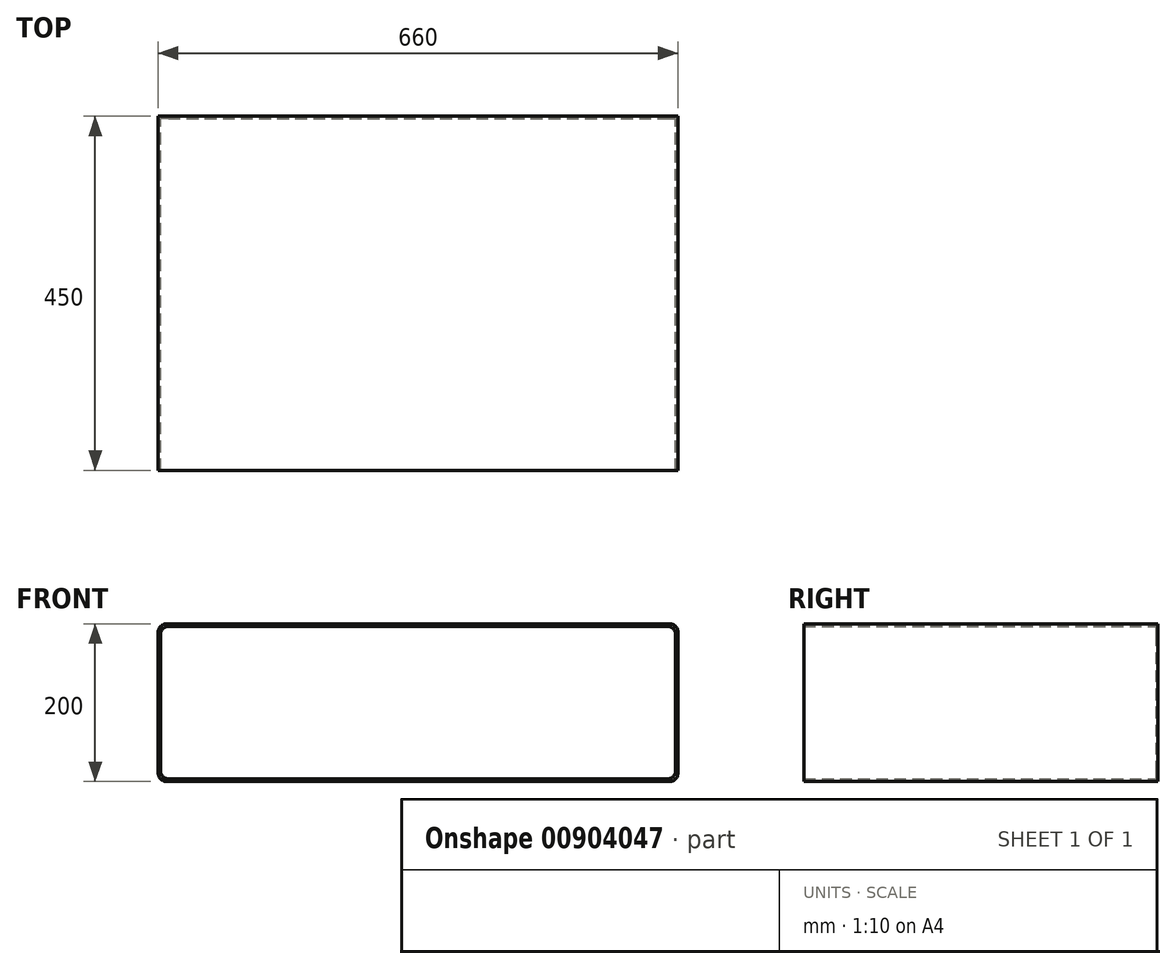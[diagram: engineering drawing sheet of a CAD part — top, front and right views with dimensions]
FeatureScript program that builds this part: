
annotation { "Feature Type Name" : "Feature", "Feature Type Description" : "" }
export const myFeature = defineFeature(function(context is Context, id is Id, definition is map)
    precondition{}
    {
        {
            assignVariable(context, id + "F0", {"name" : "Length", "anyValue" : 900});
        }
        {
            var Q0;
            Q0=qCreatedBy(makeId("Top.planeOp"),FACE);
            var sketch = newSketch(context, id + "F1", { "sketchPlane" : qUnion([Q0])});
            skLineSegment(sketch, "E0.bottom", {"start": v(-350, 450) * mm, "end": v(350, 450) * mm, "construction": true});
            skLineSegment(sketch, "E0.top", {"start": v(-350, -450) * mm, "end": v(350, -450) * mm, "construction": true});
            skLineSegment(sketch, "E0.left", {"start": v(-350, 450) * mm, "end": v(-350, -450) * mm, "construction": true});
            skLineSegment(sketch, "E0.right", {"start": v(350, 450) * mm, "end": v(350, -450) * mm, "construction": true});
            skLineSegment(sketch, "E1", {"start": v(-350, 0) * mm, "end": v(350, 0) * mm, "construction": true});
            skLineSegment(sketch, "E2", {"start": v(0, 450) * mm, "end": v(0, 0) * mm, "construction": true});
            skLineSegment(sketch, "E3", {"start": v(0, 0) * mm, "end": v(0, -450) * mm, "construction": true});
            skSolve(sketch);
        }
        {
            var Q0;
            Q0=qCreatedBy(makeId("Front.planeOp"),FACE);
            var sketch = newSketch(context, id + "F2", { "sketchPlane" : qUnion([Q0])});
            skLineSegment(sketch, "E4.bottom", {"start": v(-350, 300) * mm, "end": v(350, 300) * mm, "construction": true});
            skLineSegment(sketch, "E4.top", {"start": v(-350, -300) * mm, "end": v(350, -300) * mm, "construction": true});
            skLineSegment(sketch, "E4.left", {"start": v(-350, 300) * mm, "end": v(-350, -300) * mm, "construction": true});
            skLineSegment(sketch, "E4.right", {"start": v(350, 300) * mm, "end": v(350, -300) * mm, "construction": true});
            skLineSegment(sketch, "E5", {"start": v(0, 300) * mm, "end": v(0, -300) * mm, "construction": true});
            skSolve(sketch);
        }
        {
            var Q0;
            Q0=qCreatedBy(makeId("Front.planeOp"),FACE);
            var sketch = newSketch(context, id + "F3", { "sketchPlane" : qUnion([Q0])});
            skLineSegment(sketch, "E6.bottom", {"start": v(-330, 0) * mm, "end": v(330, 0) * mm});
            skLineSegment(sketch, "E6.top", {"start": v(-330, -200) * mm, "end": v(330, -200) * mm});
            skLineSegment(sketch, "E6.left", {"start": v(-330, 0) * mm, "end": v(-330, -200) * mm});
            skLineSegment(sketch, "E6.right", {"start": v(330, 0) * mm, "end": v(330, -200) * mm});
            skSolve(sketch);
        }
        {
            var Q0;
            Q0=makeQuery(id+"F3.imprint","IMPRINT",FACE,{"disambiguationData":[TD([[makeQuery(id+"F3.imprint","IMPRINT",EDGE,{"derivedFrom":sQuery(id+"F3.wireOp",EDGE,"E6.bottom")}),-1.0]])]});
            extrude(context, id + "F4", {"entities" : qUnion([Q0]), "depth" : (getVariable(context, 'Length') / 2) * mm, "offsetDistance" : 25 * mm});
        }
        {
            var Q0;
            Q0=makeQuery(id+"F4.opExtrude","CAP_FACE",FACE,{"disambiguationData":[OSD([sQuery(id+"F3.wireOp",EDGE,"E6.bottom"),sQuery(id+"F3.wireOp",EDGE,"E6.top"),sQuery(id+"F3.wireOp",EDGE,"E6.left"),sQuery(id+"F3.wireOp",EDGE,"E6.right")])],"isStart":false});
            shell(context, id + "F5", {"entities" : qUnion([Q0]), "thickness" : 3 * mm});
        }
        {
            var Q0;
            Q0=makeQuery(id+"F4.opExtrude","SWEPT_EDGE",EDGE,{"disambiguationData":[OSD([sQuery(id+"F3.wireOp",EDGE,"E6.top"),sQuery(id+"F3.wireOp",EDGE,"E6.right")])]});
            var Q1;
            Q1=makeQuery(id+"F4.opExtrude","SWEPT_EDGE",EDGE,{"disambiguationData":[OSD([sQuery(id+"F3.wireOp",EDGE,"E6.bottom"),sQuery(id+"F3.wireOp",EDGE,"E6.right")])]});
            fillet(context, id + "F6", {"entities" : qUnion([Q0, Q1]), "radius" : 10 * mm, "tangentPropagation" : true, "allowEdgeOverflow" : false});
        }
        {
            var Q0;
            Q0=makeQuery(id+"F5.opShell","OFFSET_EDGE",EDGE,{"disambiguationData":[OSD([sQuery(id+"F3.wireOp",EDGE,"E6.top"),sQuery(id+"F3.wireOp",EDGE,"E6.right")])]});
            var Q1;
            Q1=makeQuery(id+"F5.opShell","OFFSET_EDGE",EDGE,{"disambiguationData":[OSD([sQuery(id+"F3.wireOp",EDGE,"E6.bottom"),sQuery(id+"F3.wireOp",EDGE,"E6.right")])]});
            var Q2;
            Q2=makeQuery(id+"F5.opShell","OFFSET_EDGE",EDGE,{"disambiguationData":[OSD([sQuery(id+"F3.wireOp",EDGE,"E6.top"),sQuery(id+"F3.wireOp",EDGE,"E6.left")])]});
            var Q3;
            Q3=makeQuery(id+"F5.opShell","OFFSET_EDGE",EDGE,{"disambiguationData":[OSD([sQuery(id+"F3.wireOp",EDGE,"E6.bottom"),sQuery(id+"F3.wireOp",EDGE,"E6.left")])]});
            fillet(context, id + "F7", {"entities" : qUnion([Q0, Q1, Q2, Q3]), "radius" : 10 * mm, "tangentPropagation" : true, "allowEdgeOverflow" : false});
        }
        {
            var Q0;
            Q0=makeQuery(id+"F4.opExtrude","SWEPT_EDGE",EDGE,{"disambiguationData":[OSD([sQuery(id+"F3.wireOp",EDGE,"E6.top"),sQuery(id+"F3.wireOp",EDGE,"E6.left")])]});
            var Q1;
            Q1=makeQuery(id+"F4.opExtrude","SWEPT_EDGE",EDGE,{"disambiguationData":[OSD([sQuery(id+"F3.wireOp",EDGE,"E6.bottom"),sQuery(id+"F3.wireOp",EDGE,"E6.left")])]});
            fillet(context, id + "F8", {"entities" : qUnion([Q0, Q1]), "radius" : 10 * mm, "tangentPropagation" : true, "allowEdgeOverflow" : false});
        }
    });
